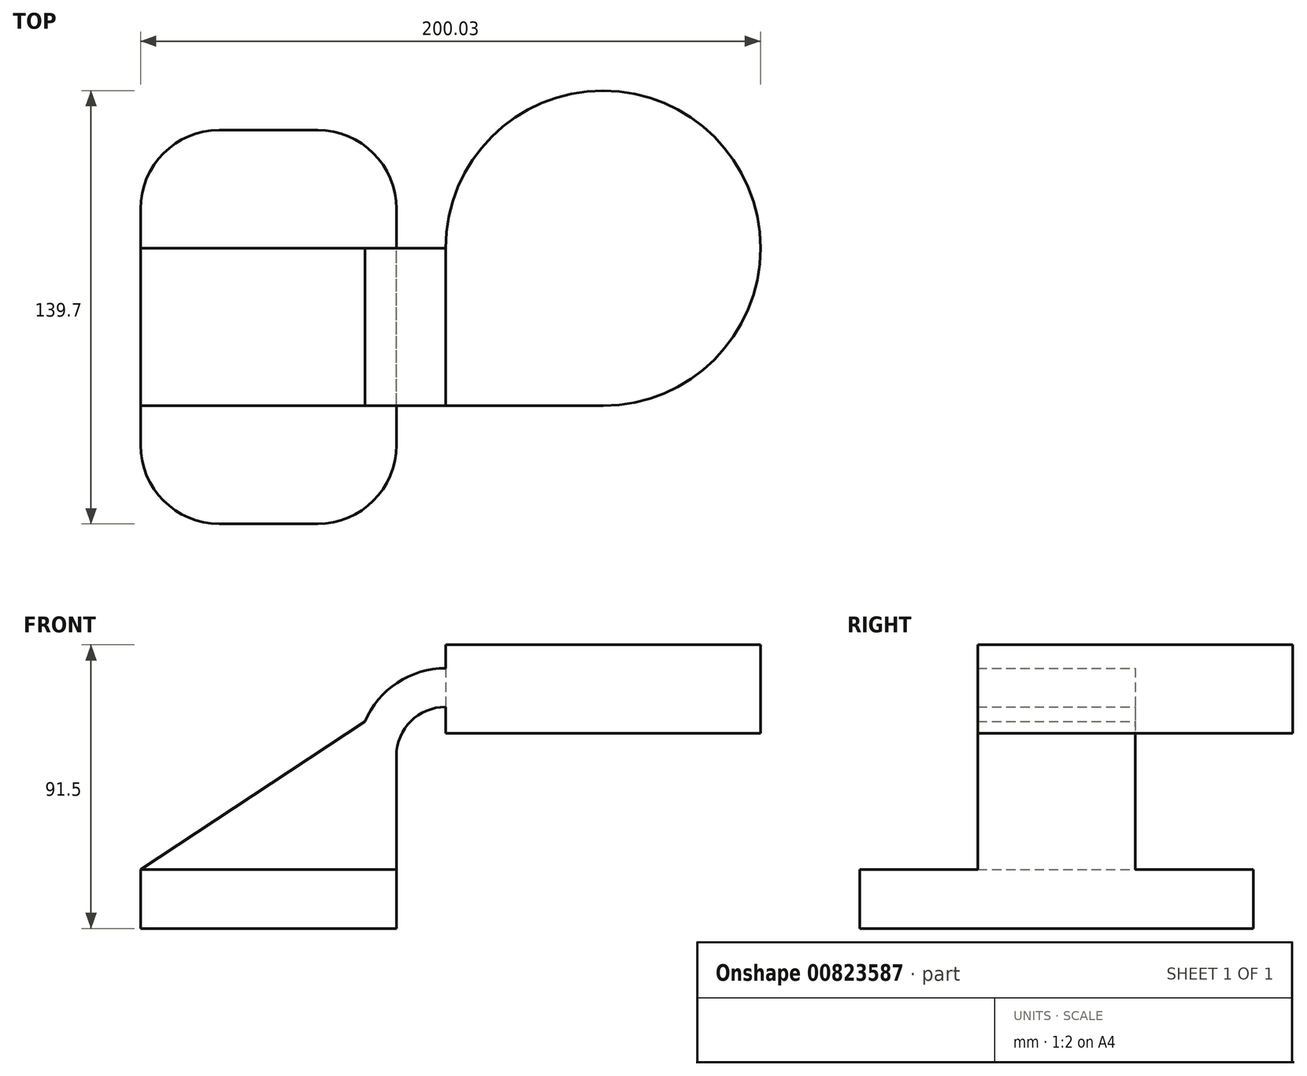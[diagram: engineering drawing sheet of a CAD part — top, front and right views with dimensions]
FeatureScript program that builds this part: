
annotation { "Feature Type Name" : "Feature", "Feature Type Description" : "" }
export const myFeature = defineFeature(function(context is Context, id is Id, definition is map)
    precondition{}
    {
        {
            var Q0;
            Q0=qCreatedBy(makeId("Front.planeOp"),FACE);
            var sketch = newSketch(context, id + "F0", { "sketchPlane" : qUnion([Q0])});
            skLineSegment(sketch, "E0.bottom", {"start": v(-41.28, 9.53) * mm, "end": v(41.28, 9.53) * mm});
            skLineSegment(sketch, "E0.top", {"start": v(-41.28, -9.53) * mm, "end": v(41.28, -9.53) * mm});
            skLineSegment(sketch, "E0.left", {"start": v(-41.28, 9.53) * mm, "end": v(-41.28, -9.53) * mm});
            skLineSegment(sketch, "E0.right", {"start": v(41.28, 9.53) * mm, "end": v(41.28, -9.53) * mm});
            skPoint(sketch, "E0.middle", {"position": v(0, 0) * mm});
            skLineSegment(sketch, "E1.bottom", {"start": v(107.95, 53.4) * mm, "end": v(57.15, 53.4) * mm});
            skLineSegment(sketch, "E1.top", {"start": v(107.95, 81.97) * mm, "end": v(57.15, 81.97) * mm});
            skLineSegment(sketch, "E1.left", {"start": v(107.95, 53.4) * mm, "end": v(107.95, 81.97) * mm});
            skLineSegment(sketch, "E1.right", {"start": v(57.15, 53.4) * mm, "end": v(57.15, 81.97) * mm});
            skPoint(sketch, "E1.middle", {"position": v(82.55, 67.68) * mm});
            skLineSegment(sketch, "E2", {"start": v(41.28, 9.53) * mm, "end": v(41.28, 46.05) * mm});
            skArc(sketch, "E3", {"start": v(41.28, 46.05) * mm, "mid": v(45.92, 57.28) * mm, "end": v(57.15, 61.93) * mm});
            skLineSegment(sketch, "E4", {"start": v(57.15, 61.93) * mm, "end": v(72.32, 61.93) * mm});
            skLineSegment(sketch, "E5.0", {"start": v(57.15, 74.4) * mm, "end": v(72.32, 74.4) * mm});
            skArc(sketch, "E5.1", {"start": v(28.8, 46.05) * mm, "mid": v(37.1, 66.1) * mm, "end": v(57.15, 74.4) * mm});
            skLineSegment(sketch, "E5.2", {"start": v(28.8, 9.53) * mm, "end": v(28.8, 46.05) * mm});
            skLineSegment(sketch, "E6", {"start": v(72.32, 74.4) * mm, "end": v(72.32, 61.93) * mm});
            skLineSegment(sketch, "E7", {"start": v(72.32, 74.4) * mm, "end": v(72.32, 81.97) * mm});
            skLineSegment(sketch, "E8", {"start": v(72.32, 61.93) * mm, "end": v(72.32, 53.4) * mm});
            skFitSpline(sketch, "E9", {"points": [v(-41.28, 9.53) * mm, v(57.15, 74.4) * mm], "startDerivative": vector(98.43, 64.88) * mm, "endDerivative": vector(98.43, 64.88) * mm});
            skFitSpline(sketch, "E10", {"points": [v(-8.47, 31.15) * mm, v(-26.48, 40.51) * mm], "startDerivative": vector(-18.01, 9.36) * mm, "endDerivative": vector(-18.01, 9.36) * mm});
            skSolve(sketch);
        }
        {
            var Q0;
            Q0=makeQuery(id+"F0.imprint","IMPRINT",FACE,{"disambiguationData":[TD([[makeQuery(id+"F0.imprint","IMPRINT",EDGE,{"derivedFrom":sQuery(id+"F0.wireOp",EDGE,"E0.top")}),1.0]])]});
            extrude(context, id + "F1", {"entities" : qUnion([Q0]), "endBound" : BoundingType.SYMMETRIC, "depth" : 127 * mm, "offsetDistance" : 25.4 * mm});
        }
        {
            var Q0;
            Q0 = qSketchRegion(id + "F0", true);
            extrude(context, id + "F2", {"entities" : qUnion([Q0]), "operationType" : NewBodyOperationType.ADD, "endBound" : BoundingType.SYMMETRIC, "depth" : 50.8 * mm, "offsetDistance" : 25.4 * mm});
        }
        {
            var Q0;
            Q0=makeQuery(id+"F2.opExtrude","SWEPT_FACE",FACE,{"disambiguationData":[OSD([sQuery(id+"F0.wireOp",EDGE,"E1.left")])]});
            var Q1;
            Q1=makeQuery(id+"F2.opExtrude","CAP_EDGE",EDGE,{"disambiguationData":[OSD([sQuery(id+"F0.wireOp",EDGE,"E1.left")])],"isStart":true});
            revolve(context, id + "F3", {"operationType" : NewBodyOperationType.ADD, "surfaceOperationType" : NewSurfaceOperationType.NEW, "entities" : qUnion([Q0]), "axis" : qUnion([Q1]), "revolveType" : RevolveType.FULL});
        }
        {
            var Q0;
            Q0=makeQuery(id+"F1.opExtrude","CAP_EDGE",EDGE,{"disambiguationData":[OSD([sQuery(id+"F0.wireOp",EDGE,"E0.right")])],"isStart":false});
            var Q1;
            Q1=makeQuery(id+"F1.opExtrude","CAP_EDGE",EDGE,{"disambiguationData":[OSD([sQuery(id+"F0.wireOp",EDGE,"E0.left")])],"isStart":false});
            fillet(context, id + "F4", {"entities" : qUnion([Q0, Q1]), "radius" : 25.4 * mm, "tangentPropagation" : true, "allowEdgeOverflow" : false});
        }
        {
            var Q0;
            Q0=makeQuery(id+"F1.opExtrude","CAP_EDGE",EDGE,{"disambiguationData":[OSD([sQuery(id+"F0.wireOp",EDGE,"E0.left")])],"isStart":true});
            var Q1;
            Q1=makeQuery(id+"F1.opExtrude","CAP_EDGE",EDGE,{"disambiguationData":[OSD([sQuery(id+"F0.wireOp",EDGE,"E0.right")])],"isStart":true});
            fillet(context, id + "F5", {"entities" : qUnion([Q0, Q1]), "radius" : 25.4 * mm, "tangentPropagation" : true, "allowEdgeOverflow" : false});
        }
    });
